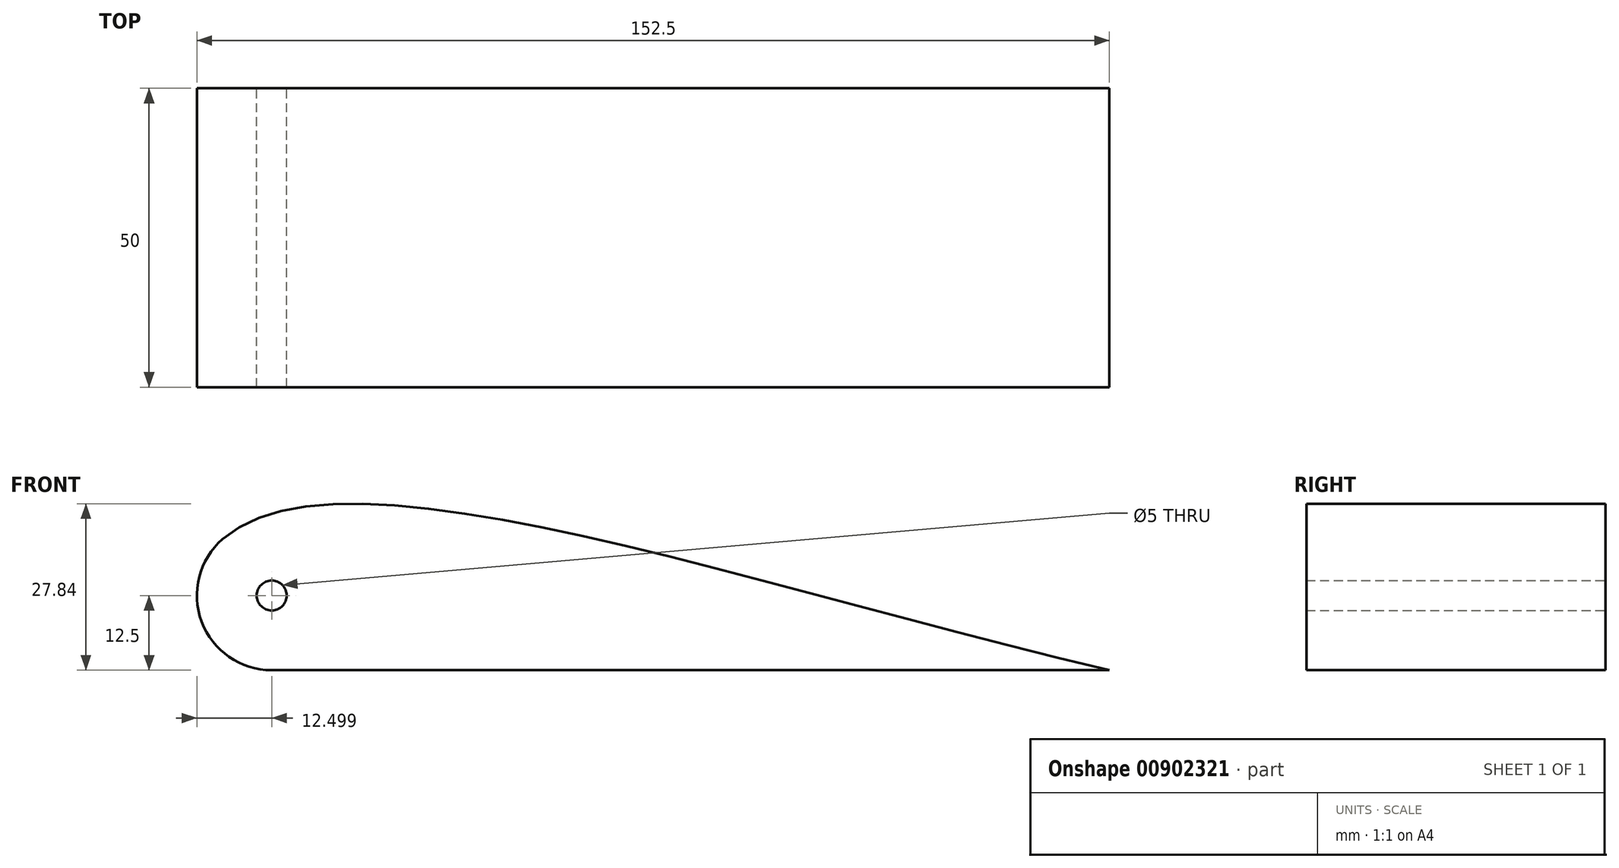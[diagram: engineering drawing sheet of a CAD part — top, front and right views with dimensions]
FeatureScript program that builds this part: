
annotation { "Feature Type Name" : "Feature", "Feature Type Description" : "" }
export const myFeature = defineFeature(function(context is Context, id is Id, definition is map)
    precondition{}
    {
        {
            var Q0;
            Q0=qCreatedBy(makeId("Front.planeOp"),FACE);
            var sketch = newSketch(context, id + "F0", { "sketchPlane" : qUnion([Q0])});
            skArc(sketch, "E0", {"start": v(-69.76, 9.43) * mm, "mid": v(-73.27, -4.38) * mm, "end": v(-61.56, -12.5) * mm});
            skLineSegment(sketch, "E1", {"start": v(-61.56, -12.5) * mm, "end": v(78.44, -12.5) * mm});
            skFitSpline(sketch, "E2", {"points": [v(78.44, -12.5) * mm, v(-69.76, 9.43) * mm, v(-68.4, -44.74) * mm], "startDerivative": vector(-315.22, 75.21) * mm, "endDerivative": vector(71.3, -154.68) * mm});
            skCircle(sketch, "E3", {"center": v(-61.56, 0) * mm, "radius": 2.5 * mm});
            skSolve(sketch);
        }
        {
            var Q0;
            Q0 = qSketchRegion(id + "F0", true);
            extrude(context, id + "F1", {"entities" : qUnion([Q0]), "endBound" : BoundingType.SYMMETRIC, "depth" : 50 * mm, "offsetDistance" : 25 * mm});
        }
    });
